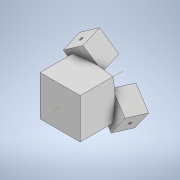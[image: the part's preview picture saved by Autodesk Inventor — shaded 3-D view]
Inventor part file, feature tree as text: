
AUTODESK INVENTOR PART (.ipt)
format: ipt  version: 2022 (Build 260153000, 153)  size: 221,696 bytes
history: native  units: mm
features: pattern_circular x6, sketch x6, extrude x5, revolve x1, plane x1
ambient origin geometry x8: Origin, YZ Plane, XZ Plane, XY Plane, X Axis, Y Axis, Z Axis, Center Point
bodies: Body1 (feature_tree), Body2 (feature_tree)
feature tree (19):
  extrude  "Extrusion3"  Depth=10.0mm
  revolve  "Revolution1"  [1 undecoded]
  plane  "Work Plane1"
  extrude  "Extrusion4"  TaperAngle=90.0deg  [1 undecoded]
  pattern_circular  "Circular Pattern1"  Count=2  [1 undecoded]
  pattern_circular  "Circular Pattern2"  Count=2  [1 undecoded]
  extrude  "Extrusion5"  Depth=5.0mm
  extrude  "Extrusion6"  Depth=5.0mm
  pattern_circular  "Circular Pattern3"  [2 undecoded]
  pattern_circular  "Circular Pattern4"  [2 undecoded]
  extrude  "Extrusion7"  Depth=0.5mm TaperAngle=0.0deg
  pattern_circular  "Circular Pattern5"  Count=2  [1 undecoded]
  pattern_circular  "Circular Pattern6"  Count=2  [1 undecoded]
  sketch  "Sketch3"  dims[d7=10.0mm d8=10.0mm]
  sketch  "Sketch8"  dims[d9=10.0mm d10=0.0mm d13=13.108049mm]
  sketch  "Sketch9"  dims[d14=15.0deg d15=90.0deg]
  sketch  "Sketch10"  dims[d16=0.75mm]
  sketch  "Sketch11"  dims[d17=2.0mm]
  sketch  "Sketch12"  dims[d18=2.0mm d19=0.0mm d20=20.0mm d21=45.378561mm d23=20.0mm d24=-45.378561mm d26=5.0mm d27=5.0mm d28=0.5mm d29=5.0mm d30=0.0mm d31=0.5mm d32=0.0mm d33=20.0mm d34=45.378561mm d36=20.0mm d37=-45.378561mm d39=0.75mm d40=2.0mm d41=2.5mm d42=0.0mm d43=0.0mm d44=20.0mm d45=45.378561mm d47=20.0mm d48=-45.378561mm]
note: 10 required parameter values undecoded (feature->parameter linkage not recoverable at this tier; creation-order binding heuristic only, values carry confidence <= 0.55)